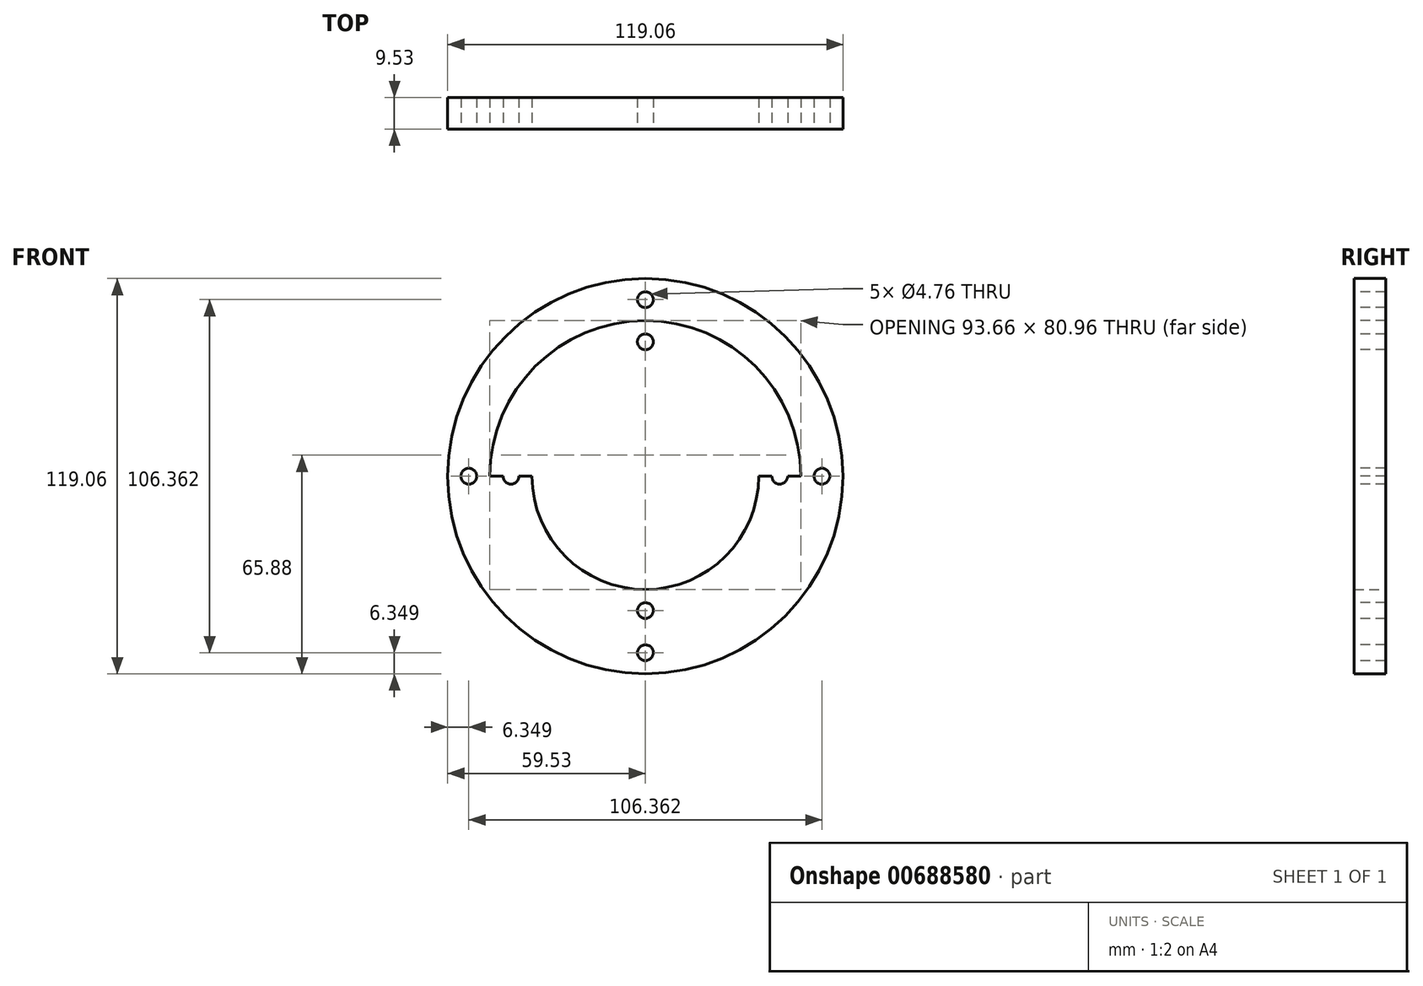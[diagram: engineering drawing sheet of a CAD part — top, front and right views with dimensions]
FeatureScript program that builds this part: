
annotation { "Feature Type Name" : "Feature", "Feature Type Description" : "" }
export const myFeature = defineFeature(function(context is Context, id is Id, definition is map)
    precondition{}
    {
        {
            var Q0;
            Q0=qCreatedBy(makeId("Front.planeOp"),FACE);
            var sketch = newSketch(context, id + "F0", { "sketchPlane" : qUnion([Q0])});
            skCircle(sketch, "E0", {"center": v(0, 0) * mm, "radius": 59.53 * mm});
            skCircle(sketch, "E1", {"center": v(0, 0) * mm, "radius": 46.83 * mm});
            skCircle(sketch, "E2", {"center": v(0, 0) * mm, "radius": 34.13 * mm});
            skSolve(sketch);
        }
        {
            var Q0;
            Q0 = qSketchRegion(id + "F0", true);
            var Q1;
            Q1=makeQuery(id+"F0.imprint","IMPRINT",FACE,{"disambiguationData":[TD([[makeQuery(id+"F0.imprint","IMPRINT",EDGE,{"derivedFrom":sQuery(id+"F0.wireOp",EDGE,"E1")}),1.0]])]});
            extrude(context, id + "F1", {"entities" : qUnion([Q0, Q1]), "depth" : 9.52 * mm, "offsetDistance" : 25.4 * mm});
        }
        {
            var Q0;
            Q0=makeQuery(id+"F1.opExtrude","CAP_FACE",FACE,{"disambiguationData":[OSD([sQuery(id+"F0.wireOp",EDGE,"E0"),sQuery(id+"F0.wireOp",EDGE,"E2")])],"isStart":false});
            var sketch = newSketch(context, id + "F2", { "sketchPlane" : qUnion([Q0])});
            skCircle(sketch, "E3", {"center": v(0, 0) * mm, "radius": 46.83 * mm});
            skLineSegment(sketch, "E4", {"start": v(-59.53, 0) * mm, "end": v(-34.13, 0) * mm});
            skLineSegment(sketch, "E5", {"start": v(0, 59.53) * mm, "end": v(0, 34.13) * mm});
            skLineSegment(sketch, "E6", {"start": v(34.13, 0) * mm, "end": v(59.53, 0) * mm});
            skLineSegment(sketch, "E7", {"start": v(0, -34.13) * mm, "end": v(0, -59.53) * mm});
            skCircle(sketch, "E8", {"center": v(-53.18, 0) * mm, "radius": 2.38 * mm});
            skCircle(sketch, "E9", {"center": v(-40.48, 0) * mm, "radius": 2.38 * mm});
            skCircle(sketch, "E10", {"center": v(0, 53.18) * mm, "radius": 2.38 * mm});
            skCircle(sketch, "E11", {"center": v(0, 40.48) * mm, "radius": 2.38 * mm});
            skCircle(sketch, "E12", {"center": v(40.48, 0) * mm, "radius": 2.38 * mm});
            skCircle(sketch, "E13", {"center": v(53.18, 0) * mm, "radius": 2.38 * mm});
            skCircle(sketch, "E14", {"center": v(0, -40.48) * mm, "radius": 2.38 * mm});
            skCircle(sketch, "E15", {"center": v(0, -53.18) * mm, "radius": 2.38 * mm});
            skSolve(sketch);
        }
        {
            var Q0;
            {var subQ0=sQuery(id+"F2.wireOp",EDGE,"E12");var subQ1=sQuery(id+"F2.wireOp",EDGE,"E6");var subQ2=makeQuery(id+"F2.imprint","INTERSECT",VERTEX,{"disambiguationData":[OD(0.0)],"derivedFrom":[subQ1,subQ0]});Q0=makeQuery(id+"F2.imprint","IMPRINT",FACE,{"disambiguationData":[TD([[makeQuery(id+"F2.imprint","IMPRINT",EDGE,{"disambiguationData":[TD([[subQ2,-1.0]])],"derivedFrom":subQ1}),1.0]])]});}
            var Q1;
            {var subQ0=sQuery(id+"F2.wireOp",EDGE,"E12");var subQ1=sQuery(id+"F2.wireOp",EDGE,"E6");var subQ2=makeQuery(id+"F2.imprint","INTERSECT",VERTEX,{"disambiguationData":[OD(0.0)],"derivedFrom":[subQ1,subQ0]});Q1=makeQuery(id+"F2.imprint","IMPRINT",FACE,{"disambiguationData":[TD([[makeQuery(id+"F2.imprint","IMPRINT",EDGE,{"disambiguationData":[TD([[subQ2,-1.0]])],"derivedFrom":subQ1}),-1.0]])]});}
            var Q2;
            {var subQ0=sQuery(id+"F2.wireOp",EDGE,"E13");var subQ1=sQuery(id+"F2.wireOp",EDGE,"E6");var subQ2=makeQuery(id+"F2.imprint","INTERSECT",VERTEX,{"disambiguationData":[OD(0.0)],"derivedFrom":[subQ1,subQ0]});Q2=makeQuery(id+"F2.imprint","IMPRINT",FACE,{"disambiguationData":[TD([[makeQuery(id+"F2.imprint","IMPRINT",EDGE,{"disambiguationData":[TD([[subQ2,-1.0]])],"derivedFrom":subQ1}),1.0]])]});}
            var Q3;
            {var subQ0=sQuery(id+"F2.wireOp",EDGE,"E13");var subQ1=sQuery(id+"F2.wireOp",EDGE,"E6");var subQ2=makeQuery(id+"F2.imprint","INTERSECT",VERTEX,{"disambiguationData":[OD(0.0)],"derivedFrom":[subQ1,subQ0]});Q3=makeQuery(id+"F2.imprint","IMPRINT",FACE,{"disambiguationData":[TD([[makeQuery(id+"F2.imprint","IMPRINT",EDGE,{"disambiguationData":[TD([[subQ2,-1.0]])],"derivedFrom":subQ1}),-1.0]])]});}
            var Q4;
            {var subQ0=sQuery(id+"F2.wireOp",EDGE,"E14");var subQ1=sQuery(id+"F2.wireOp",EDGE,"E7");var subQ2=makeQuery(id+"F2.imprint","INTERSECT",VERTEX,{"disambiguationData":[OD(0.0)],"derivedFrom":[subQ1,subQ0]});Q4=makeQuery(id+"F2.imprint","IMPRINT",FACE,{"disambiguationData":[TD([[makeQuery(id+"F2.imprint","IMPRINT",EDGE,{"disambiguationData":[TD([[subQ2,-1.0]])],"derivedFrom":subQ1}),-1.0]])]});}
            var Q5;
            {var subQ0=sQuery(id+"F2.wireOp",EDGE,"E14");var subQ1=sQuery(id+"F2.wireOp",EDGE,"E7");var subQ2=makeQuery(id+"F2.imprint","INTERSECT",VERTEX,{"disambiguationData":[OD(0.0)],"derivedFrom":[subQ1,subQ0]});Q5=makeQuery(id+"F2.imprint","IMPRINT",FACE,{"disambiguationData":[TD([[makeQuery(id+"F2.imprint","IMPRINT",EDGE,{"disambiguationData":[TD([[subQ2,-1.0]])],"derivedFrom":subQ1}),1.0]])]});}
            var Q6;
            {var subQ0=sQuery(id+"F2.wireOp",EDGE,"E15");var subQ1=sQuery(id+"F2.wireOp",EDGE,"E7");var subQ2=makeQuery(id+"F2.imprint","INTERSECT",VERTEX,{"disambiguationData":[OD(0.0)],"derivedFrom":[subQ1,subQ0]});Q6=makeQuery(id+"F2.imprint","IMPRINT",FACE,{"disambiguationData":[TD([[makeQuery(id+"F2.imprint","IMPRINT",EDGE,{"disambiguationData":[TD([[subQ2,-1.0]])],"derivedFrom":subQ1}),-1.0]])]});}
            var Q7;
            {var subQ0=sQuery(id+"F2.wireOp",EDGE,"E15");var subQ1=sQuery(id+"F2.wireOp",EDGE,"E7");var subQ2=makeQuery(id+"F2.imprint","INTERSECT",VERTEX,{"disambiguationData":[OD(0.0)],"derivedFrom":[subQ1,subQ0]});Q7=makeQuery(id+"F2.imprint","IMPRINT",FACE,{"disambiguationData":[TD([[makeQuery(id+"F2.imprint","IMPRINT",EDGE,{"disambiguationData":[TD([[subQ2,-1.0]])],"derivedFrom":subQ1}),1.0]])]});}
            var Q8;
            {var subQ0=sQuery(id+"F2.wireOp",EDGE,"E9");var subQ1=sQuery(id+"F2.wireOp",EDGE,"E4");var subQ2=makeQuery(id+"F2.imprint","INTERSECT",VERTEX,{"disambiguationData":[OD(0.0)],"derivedFrom":[subQ1,subQ0]});Q8=makeQuery(id+"F2.imprint","IMPRINT",FACE,{"disambiguationData":[TD([[makeQuery(id+"F2.imprint","IMPRINT",EDGE,{"disambiguationData":[TD([[subQ2,-1.0]])],"derivedFrom":subQ1}),1.0]])]});}
            var Q9;
            {var subQ0=sQuery(id+"F2.wireOp",EDGE,"E9");var subQ1=sQuery(id+"F2.wireOp",EDGE,"E4");var subQ2=makeQuery(id+"F2.imprint","INTERSECT",VERTEX,{"disambiguationData":[OD(0.0)],"derivedFrom":[subQ1,subQ0]});Q9=makeQuery(id+"F2.imprint","IMPRINT",FACE,{"disambiguationData":[TD([[makeQuery(id+"F2.imprint","IMPRINT",EDGE,{"disambiguationData":[TD([[subQ2,-1.0]])],"derivedFrom":subQ1}),-1.0]])]});}
            var Q10;
            {var subQ0=sQuery(id+"F2.wireOp",EDGE,"E8");var subQ1=sQuery(id+"F2.wireOp",EDGE,"E4");var subQ2=makeQuery(id+"F2.imprint","INTERSECT",VERTEX,{"disambiguationData":[OD(0.0)],"derivedFrom":[subQ1,subQ0]});Q10=makeQuery(id+"F2.imprint","IMPRINT",FACE,{"disambiguationData":[TD([[makeQuery(id+"F2.imprint","IMPRINT",EDGE,{"disambiguationData":[TD([[subQ2,-1.0]])],"derivedFrom":subQ1}),1.0]])]});}
            var Q11;
            {var subQ0=sQuery(id+"F2.wireOp",EDGE,"E8");var subQ1=sQuery(id+"F2.wireOp",EDGE,"E4");var subQ2=makeQuery(id+"F2.imprint","INTERSECT",VERTEX,{"disambiguationData":[OD(0.0)],"derivedFrom":[subQ1,subQ0]});Q11=makeQuery(id+"F2.imprint","IMPRINT",FACE,{"disambiguationData":[TD([[makeQuery(id+"F2.imprint","IMPRINT",EDGE,{"disambiguationData":[TD([[subQ2,-1.0]])],"derivedFrom":subQ1}),-1.0]])]});}
            var Q12;
            {var subQ0=sQuery(id+"F2.wireOp",EDGE,"E10");var subQ1=sQuery(id+"F2.wireOp",EDGE,"E5");var subQ2=makeQuery(id+"F2.imprint","INTERSECT",VERTEX,{"disambiguationData":[OD(0.0)],"derivedFrom":[subQ1,subQ0]});Q12=makeQuery(id+"F2.imprint","IMPRINT",FACE,{"disambiguationData":[TD([[makeQuery(id+"F2.imprint","IMPRINT",EDGE,{"disambiguationData":[TD([[subQ2,-1.0]])],"derivedFrom":subQ1}),-1.0]])]});}
            var Q13;
            {var subQ0=sQuery(id+"F2.wireOp",EDGE,"E10");var subQ1=sQuery(id+"F2.wireOp",EDGE,"E5");var subQ2=makeQuery(id+"F2.imprint","INTERSECT",VERTEX,{"disambiguationData":[OD(0.0)],"derivedFrom":[subQ1,subQ0]});Q13=makeQuery(id+"F2.imprint","IMPRINT",FACE,{"disambiguationData":[TD([[makeQuery(id+"F2.imprint","IMPRINT",EDGE,{"disambiguationData":[TD([[subQ2,-1.0]])],"derivedFrom":subQ1}),1.0]])]});}
            var Q14;
            {var subQ0=sQuery(id+"F2.wireOp",EDGE,"E11");var subQ1=sQuery(id+"F2.wireOp",EDGE,"E5");var subQ2=makeQuery(id+"F2.imprint","INTERSECT",VERTEX,{"disambiguationData":[OD(0.0)],"derivedFrom":[subQ1,subQ0]});Q14=makeQuery(id+"F2.imprint","IMPRINT",FACE,{"disambiguationData":[TD([[makeQuery(id+"F2.imprint","IMPRINT",EDGE,{"disambiguationData":[TD([[subQ2,-1.0]])],"derivedFrom":subQ1}),1.0]])]});}
            var Q15;
            {var subQ0=sQuery(id+"F2.wireOp",EDGE,"E11");var subQ1=sQuery(id+"F2.wireOp",EDGE,"E5");var subQ2=makeQuery(id+"F2.imprint","INTERSECT",VERTEX,{"disambiguationData":[OD(0.0)],"derivedFrom":[subQ1,subQ0]});Q15=makeQuery(id+"F2.imprint","IMPRINT",FACE,{"disambiguationData":[TD([[makeQuery(id+"F2.imprint","IMPRINT",EDGE,{"disambiguationData":[TD([[subQ2,-1.0]])],"derivedFrom":subQ1}),-1.0]])]});}
            extrude(context, id + "F3", {"entities" : qUnion([Q0, Q1, Q2, Q3, Q4, Q5, Q6, Q7, Q8, Q9, Q10, Q11, Q12, Q13, Q14, Q15]), "operationType" : NewBodyOperationType.REMOVE, "oppositeDirection" : true, "depth" : 25.4 * mm, "offsetDistance" : 25.4 * mm});
        }
    });
